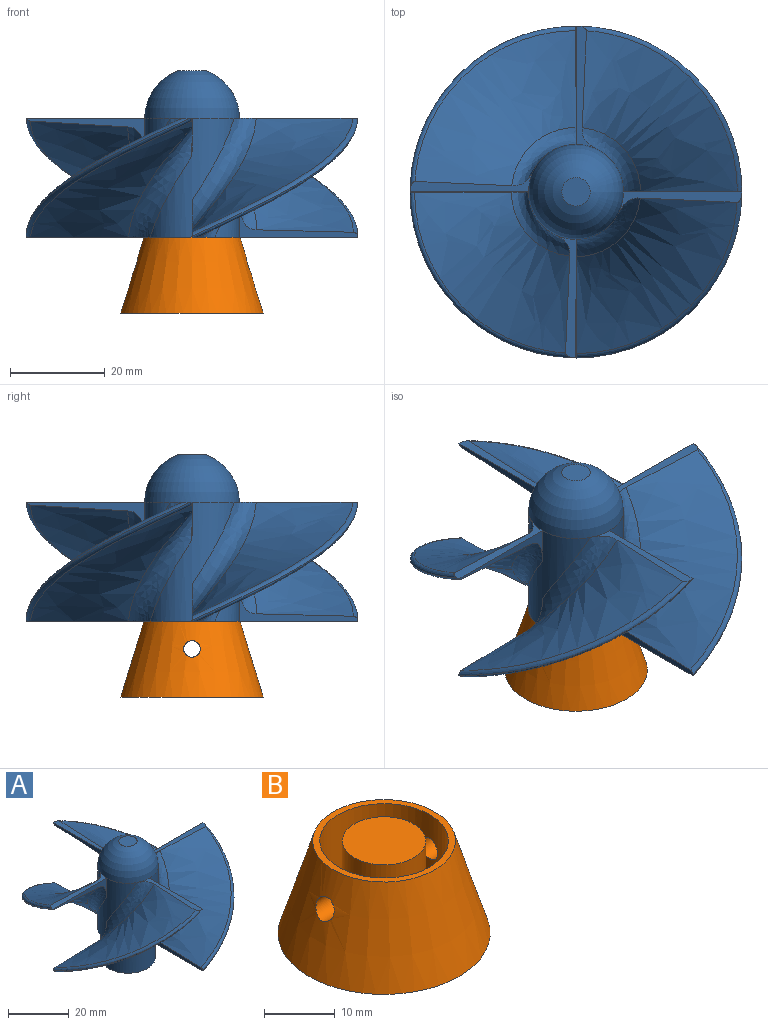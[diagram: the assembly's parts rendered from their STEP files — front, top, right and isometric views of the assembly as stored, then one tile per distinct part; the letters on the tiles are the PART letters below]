
ASSEMBLY  parts=2 mates=1
PART A: 59 faces, bbox 72.2x72.2x49.1 mm
  f0: cylinder r=6mm len=12mm, axis (0,0,1), area 400.6mm2, adj f45,f46,f47,f48,f49,f50,f51,f52
  f1: cylinder r=9mm len=18mm, axis (0,0,1), area 627.9mm2, adj f34,f45,f47,f48,f49,f50,f51,f52
  f2: plane 26.53x5.03mm, normal (0,0,1), area 46.3mm2, adj f5,f17,f18,f25,f36,f44
  f3: plane 26.53x5.03mm, normal (0,0,1), area 46.6mm2, adj f6,f19,f20,f26,f38,f44
  f4: plane 26.53x5.03mm, normal (0,0,1), area 46.3mm2, adj f7,f21,f22,f27,f40,f44
  f5: bspline ~37.39x36.09mm, area 72.9mm2, adj f2,f9,f10,f17,f25,f34
  f6: bspline ~37.39x36.09mm, area 72.9mm2, adj f3,f11,f12,f19,f26,f34
  f7: bspline ~37.39x36.09mm, area 72.9mm2, adj f4,f13,f14,f21,f27,f34
  f8: bspline ~37.39x36.09mm, area 72.9mm2, adj f15,f16,f23,f28,f33,f34
  f9: plane 25.11x7.76mm, normal (0,-1,0), area 36.8mm2, adj f5,f18,f25,f32,f34,f36
  f10: bspline ~35x35mm, area 889.3mm2, adj f5,f17,f34,f35
  f11: plane 25.11x7.76mm, normal (1,0,0), area 36.8mm2, adj f6,f20,f26,f29,f34,f38
  f12: bspline ~35x35mm, area 889.3mm2, adj f6,f19,f34,f37
  f13: plane 25.11x7.76mm, normal (0,1,0), area 36.8mm2, adj f7,f22,f27,f30,f34,f40
  f14: bspline ~35x35mm, area 889.3mm2, adj f7,f21,f34,f39
  f15: plane 25.11x7.76mm, normal (-1,0,0), area 36.8mm2, adj f8,f24,f28,f31,f34,f42
  f16: bspline ~35x35mm, area 889.3mm2, adj f8,f23,f34,f41
  f17: plane 26.95x9.96mm, normal (-1,0,0), area 35.3mm2, adj f2,f5,f10,f29,f35
  f18: bspline ~35x35mm, area 878.5mm2, adj f2,f9,f25,f36
  f19: plane 26.95x9.96mm, normal (0,-1,0), area 35.3mm2, adj f3,f6,f12,f30,f37
  f20: bspline ~35x35mm, area 878.5mm2, adj f3,f11,f26,f38
  f21: plane 26.95x9.96mm, normal (1,0,0), area 35.3mm2, adj f4,f7,f14,f31,f39
  f22: bspline ~35x35mm, area 878.5mm2, adj f4,f13,f27,f40
  f23: plane 26.95x9.96mm, normal (0,1,0), area 35.3mm2, adj f8,f16,f32,f33,f41
  f24: bspline ~35x35mm, area 878.5mm2, adj f15,f28,f33,f42
  f25: bspline ~42.24x36.24mm, area 73.8mm2, adj f2,f5,f9,f18
  f26: bspline ~42.24x36.24mm, area 73.8mm2, adj f3,f6,f11,f20
  f27: bspline ~42.24x36.24mm, area 73.8mm2, adj f4,f7,f13,f22
  f28: bspline ~42.24x36.24mm, area 73.8mm2, adj f8,f15,f24,f33
  f29: cylinder r=10mm len=25mm, axis (0,0,-1), area 187.2mm2, adj f11,f17,f34,f35,f38,f44
  f30: cylinder r=10mm len=25mm, axis (0,0,-1), area 187.2mm2, adj f13,f19,f34,f37,f40,f44
  f31: cylinder r=10mm len=25mm, axis (0,0,-1), area 187.2mm2, adj f15,f21,f34,f39,f42,f44
  f32: cylinder r=10mm len=25mm, axis (0,0,-1), area 187.2mm2, adj f9,f23,f34,f36,f41,f44
  f33: plane 26.53x5.03mm, normal (0,0,1), area 46.3mm2, adj f8,f23,f24,f28,f42,f44
  f34: plane 70.76x70.76mm, normal (0,0,-1), area 225.9mm2, adj f1,f5,f6,f7,f8,f9,f10,f11
  f35: bspline ~28.41x16.56mm, area 136.4mm2, adj f10,f17,f29,f34
  f36: bspline ~26.12x15.73mm, area 147.9mm2, adj f2,f9,f18,f32,f44
  f37: bspline ~28.41x16.56mm, area 136.4mm2, adj f12,f19,f30,f34
  f38: bspline ~26.12x15.73mm, area 147.9mm2, adj f3,f11,f20,f29,f44
  f39: bspline ~28.41x16.56mm, area 136.4mm2, adj f14,f21,f31,f34
  f40: bspline ~26.12x15.73mm, area 147.9mm2, adj f4,f13,f22,f30,f44
  f41: bspline ~28.41x16.56mm, area 136.4mm2, adj f16,f23,f32,f34
  f42: bspline ~26.12x15.73mm, area 147.9mm2, adj f15,f24,f31,f33,f44
  f43: plane 6x6mm, normal (0,0,1), area 28.3mm2, adj f44
  f44: revolved ~20x20mm, area 616.2mm2, adj f2,f3,f4,f29,f30,f31,f32,f33
  f45: plane 18x18mm, normal (0,0,-1), area 141.4mm2, adj f0,f1
  f46: plane 12x12mm, normal (0,0,-1), area 113.1mm2, adj f0
  f47: plane 3.8x2.76mm, normal (0,0.87,-0.5), area 9.8mm2, adj f0,f1,f48,f52
  f48: plane 3.21x3.1mm, normal (0,0,-1), area 9.4mm2, adj f0,f1,f47,f49
  f49: plane 3.81x2.77mm, normal (0,-0.87,-0.5), area 9.8mm2, adj f0,f1,f48,f50
  f50: plane 3.81x2.77mm, normal (0,-0.87,0.5), area 9.8mm2, adj f0,f1,f49,f51
  f51: plane 3.21x3.1mm, normal (0,0,1), area 9.4mm2, adj f0,f1,f50,f52
  f52: plane 3.8x2.76mm, normal (0,0.87,0.5), area 9.8mm2, adj f0,f1,f47,f51
  f53: plane 3.8x2.76mm, normal (0,0.87,-0.5), area 9.8mm2, adj f0,f1,f54,f58
  f54: plane 3.21x3.1mm, normal (0,0,-1), area 9.4mm2, adj f0,f1,f53,f55
  f55: plane 3.81x2.77mm, normal (0,-0.87,-0.5), area 9.8mm2, adj f0,f1,f54,f56
  f56: plane 3.81x2.77mm, normal (0,-0.87,0.5), area 9.8mm2, adj f0,f1,f55,f57
  f57: plane 3.21x3.1mm, normal (0,0,1), area 9.4mm2, adj f0,f1,f56,f58
  f58: plane 3.8x2.76mm, normal (0,0.87,0.5), area 9.8mm2, adj f0,f1,f53,f57
PART B: 15 faces, bbox 30x30x16 mm
  f0: cylinder r=1.75mm len=4.05mm, axis (1,0,0), area 41mm2, adj f1,f11,f12,f13
  f1: cylinder r=5.9mm len=12mm, axis (0,0,1), area 425.4mm2, adj f0,f2,f7,f10
  f2: plane 11.8x11.8mm, normal (0,0,1), area 109.4mm2, adj f1
  f3: plane 30x30mm, normal (0,0,-1), area 687.3mm2, adj f4,f11,f13
  f4: cone r=15mm half-angle=17deg, axis (0,0,-1), area 1299.3mm2, adj f3,f5,f8,f9
  f5: plane 20.2x20.2mm, normal (0,0,1), area 60.3mm2, adj f4,f6
  f6: cylinder r=9.1mm len=18.2mm, axis (0,0,1), area 666.7mm2, adj f5,f7,f8,f9
  f7: plane 18.2x18.2mm, normal (0,0,1), area 150.8mm2, adj f1,f6
  f8: cylinder r=1.75mm len=3.51mm, axis (1,0,0), area 31mm2, adj f4,f6
  f9: cylinder r=1.75mm len=3.51mm, axis (1,0,0), area 31mm2, adj f4,f6
  f10: cylinder r=1.75mm len=4.06mm, axis (1,0,0), area 39.1mm2, adj f1,f13
  f11: plane 9.16x2.89mm, normal (1,0,0), area 24.9mm2, adj f0,f3,f13
  f12: plane 4.4x2.89mm, normal (1,0,0), area 11.1mm2, adj f0,f13,f14
  f13: cylinder r=2.55mm len=15.5mm, axis (0,0,-1), area 189.3mm2, adj f0,f3,f10,f11,f12,f14
  f14: plane 5.1x4.65mm, normal (0,0,-1), area 19.5mm2, adj f12,f13
PLACE A at identity
PLACE B t=(0,0,0.09)mm
MATE fastened B.f1 <-> A.f0  axis (0,0,1) through (0,0,0)mm
